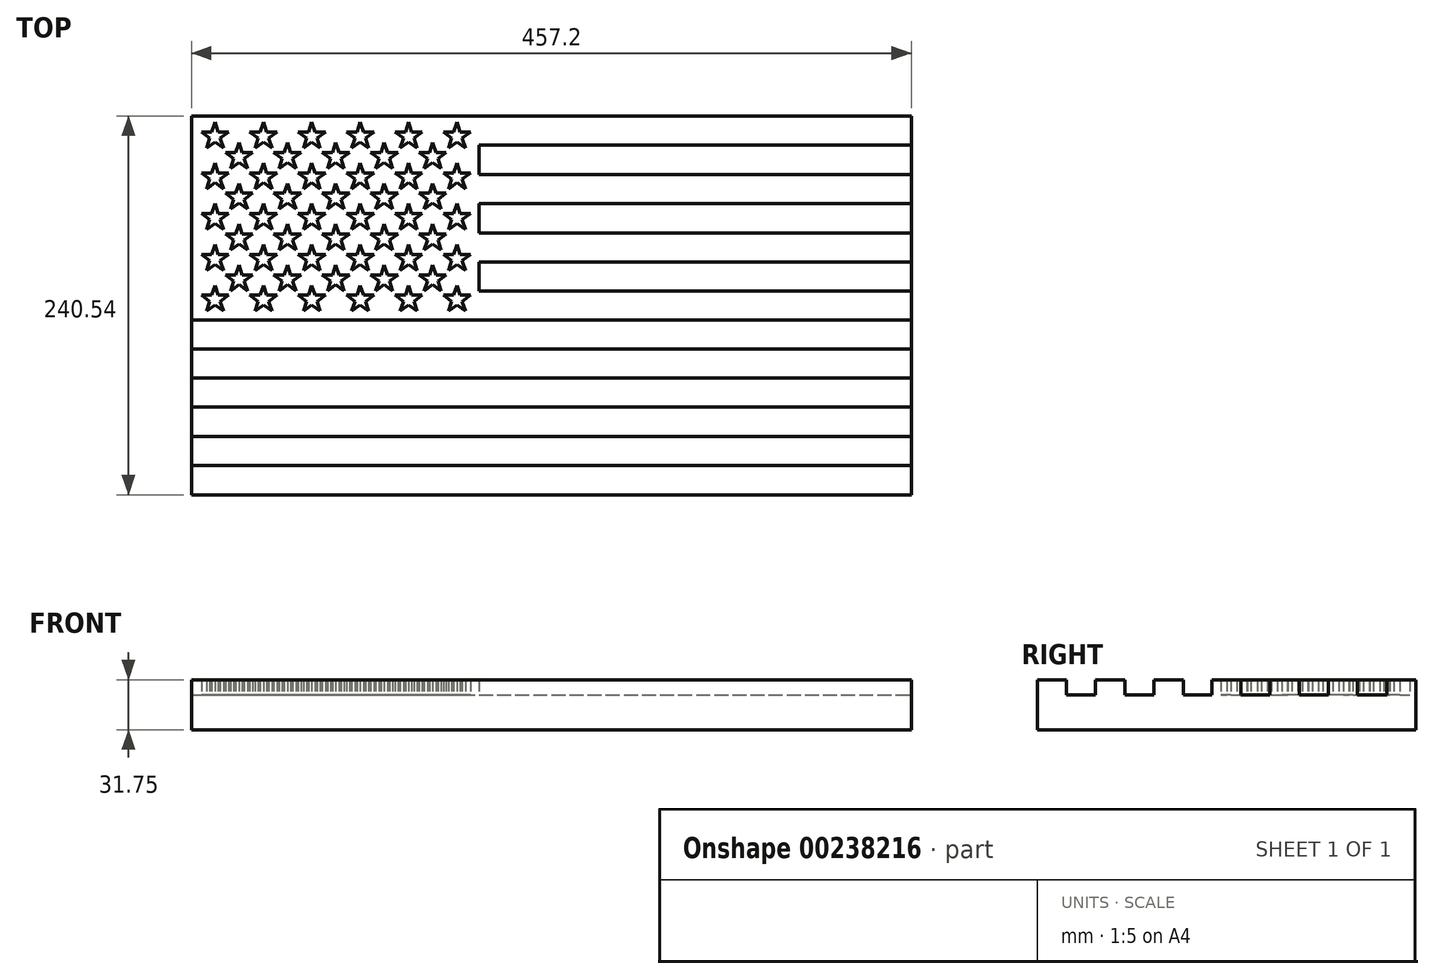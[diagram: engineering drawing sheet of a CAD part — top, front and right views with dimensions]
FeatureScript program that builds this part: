
annotation { "Feature Type Name" : "Feature", "Feature Type Description" : "" }
export const myFeature = defineFeature(function(context is Context, id is Id, definition is map)
    precondition{}
    {
        {
            var Q0;
            Q0=qCreatedBy(makeId("Top.planeOp"),FACE);
            var sketch = newSketch(context, id + "F0", { "sketchPlane" : qUnion([Q0])});
            skLineSegment(sketch, "E0.rect.bottom", {"start": v(228.6, 120.27) * mm, "end": v(-228.6, 120.27) * mm});
            skLineSegment(sketch, "E0.rect.top", {"start": v(228.6, -120.27) * mm, "end": v(-228.6, -120.27) * mm});
            skLineSegment(sketch, "E0.rect.left", {"start": v(228.6, 120.27) * mm, "end": v(228.6, -120.27) * mm});
            skLineSegment(sketch, "E0.rect.right", {"start": v(-228.6, 120.27) * mm, "end": v(-228.6, -120.27) * mm});
            skPoint(sketch, "E0.rect.middle", {"position": v(0, 0) * mm});
            skSolve(sketch);
        }
        {
            var Q0;
            Q0=qSketchRegion(id+"F0",true);
            extrude(context, id + "F1", {"entities" : qUnion([Q0]), "depth" : 22.22 * mm});
        }
        {
            var Q0;
            Q0=makeQuery(id+"F1.opExtrude","CAP_FACE",FACE,{"disambiguationData":[OSD([sQuery(id+"F0.wireOp",EDGE,"E0.rect.bottom"),sQuery(id+"F0.wireOp",EDGE,"E0.rect.top"),sQuery(id+"F0.wireOp",EDGE,"E0.rect.left"),sQuery(id+"F0.wireOp",EDGE,"E0.rect.right")])],"isStart":false});
            var sketch = newSketch(context, id + "F2", { "sketchPlane" : qUnion([Q0])});
            skLineSegment(sketch, "E1.bottom", {"start": v(-228.6, 120.27) * mm, "end": v(-45.97, 120.27) * mm});
            skLineSegment(sketch, "E1.top", {"start": v(-228.6, -9.25) * mm, "end": v(-45.97, -9.25) * mm});
            skLineSegment(sketch, "E1.left", {"start": v(-228.6, 120.27) * mm, "end": v(-228.6, -9.25) * mm});
            skLineSegment(sketch, "E1.right", {"start": v(-45.97, 120.27) * mm, "end": v(-45.97, -9.25) * mm});
            skLineSegment(sketch, "E2.bottom", {"start": v(-45.97, 120.27) * mm, "end": v(228.6, 120.27) * mm});
            skLineSegment(sketch, "E2.top", {"start": v(-45.97, 101.73) * mm, "end": v(228.6, 101.73) * mm});
            skLineSegment(sketch, "E2.left", {"start": v(-45.97, 120.27) * mm, "end": v(-45.97, 101.73) * mm});
            skLineSegment(sketch, "E2.right", {"start": v(228.6, 120.27) * mm, "end": v(228.6, 101.73) * mm});
            skLineSegment(sketch, "E3.MirrorCS", {"start": v(-45.97, 83.19) * mm, "end": v(228.6, 83.19) * mm});
            skLineSegment(sketch, "E4.MirrorCS", {"start": v(-45.97, 64.64) * mm, "end": v(228.6, 64.64) * mm});
            skLineSegment(sketch, "E5.MirrorCS", {"start": v(-45.97, 46.1) * mm, "end": v(228.6, 46.1) * mm});
            skLineSegment(sketch, "E6.MirrorCS", {"start": v(-45.97, 27.56) * mm, "end": v(228.6, 27.56) * mm});
            skLineSegment(sketch, "E7.MirrorCS", {"start": v(-45.97, 9.02) * mm, "end": v(228.6, 9.02) * mm});
            skLineSegment(sketch, "E8", {"start": v(-45.97, -9.25) * mm, "end": v(228.6, -9.25) * mm});
            skLineSegment(sketch, "E9.bottom", {"start": v(-228.6, -120.27) * mm, "end": v(228.6, -120.27) * mm});
            skLineSegment(sketch, "E9.top", {"start": v(-228.6, -101.73) * mm, "end": v(228.6, -101.73) * mm});
            skLineSegment(sketch, "E9.left", {"start": v(-228.6, -120.27) * mm, "end": v(-228.6, -101.73) * mm});
            skLineSegment(sketch, "E9.right", {"start": v(228.6, -120.27) * mm, "end": v(228.6, -101.73) * mm});
            skLineSegment(sketch, "E10.MirrorCS", {"start": v(-228.6, -83.19) * mm, "end": v(228.6, -83.19) * mm});
            skLineSegment(sketch, "E11.MirrorCS", {"start": v(-228.6, -64.64) * mm, "end": v(228.6, -64.64) * mm});
            skLineSegment(sketch, "E12.MirrorCS", {"start": v(-228.6, -46.1) * mm, "end": v(228.6, -46.1) * mm});
            skLineSegment(sketch, "E13.MirrorCS", {"start": v(-228.6, -27.56) * mm, "end": v(228.6, -27.56) * mm});
            skLineSegment(sketch, "E14.bottom", {"start": v(-228.6, 120.27) * mm, "end": v(-213.61, 120.27) * mm});
            skLineSegment(sketch, "E14.left", {"start": v(-228.6, 120.27) * mm, "end": v(-228.6, 107.31) * mm});
            skLineSegment(sketch, "E15.trimOffspring", {"start": v(-210.03, 108.18) * mm, "end": v(-210.03, 108.18) * mm});
            skLineSegment(sketch, "E16", {"start": v(-222.27, 110.13) * mm, "end": v(-215.66, 110.13) * mm});
            skLineSegment(sketch, "E17", {"start": v(-204.95, 110.13) * mm, "end": v(-210.3, 106.24) * mm});
            skLineSegment(sketch, "E18", {"start": v(-218.97, 99.95) * mm, "end": v(-216.92, 106.24) * mm});
            skLineSegment(sketch, "E19", {"start": v(-213.61, 116.42) * mm, "end": v(-211.57, 110.13) * mm});
            skLineSegment(sketch, "E20", {"start": v(-208.26, 99.95) * mm, "end": v(-213.61, 103.84) * mm});
            skLineSegment(sketch, "E21.trimOffspring", {"start": v(-210.3, 106.24) * mm, "end": v(-208.26, 99.95) * mm});
            skLineSegment(sketch, "E22.trimOffspring", {"start": v(-211.57, 110.13) * mm, "end": v(-204.95, 110.13) * mm});
            skLineSegment(sketch, "E23.trimOffspring", {"start": v(-215.66, 110.13) * mm, "end": v(-213.61, 116.42) * mm});
            skLineSegment(sketch, "E24.trimOffspring", {"start": v(-216.92, 106.24) * mm, "end": v(-222.27, 110.13) * mm});
            skLineSegment(sketch, "E25.trimOffspring", {"start": v(-213.61, 103.84) * mm, "end": v(-218.97, 99.95) * mm});
            skLineSegment(sketch, "E26.0.1.0", {"start": v(-218.97, 74.04) * mm, "end": v(-216.92, 80.33) * mm});
            skLineSegment(sketch, "E26.0.1.1", {"start": v(-210.3, 80.33) * mm, "end": v(-208.26, 74.04) * mm});
            skLineSegment(sketch, "E26.0.1.2", {"start": v(-211.57, 84.22) * mm, "end": v(-204.95, 84.22) * mm});
            skLineSegment(sketch, "E26.0.1.3", {"start": v(-216.92, 80.33) * mm, "end": v(-222.27, 84.22) * mm});
            skLineSegment(sketch, "E26.0.1.4", {"start": v(-213.61, 77.93) * mm, "end": v(-218.97, 74.04) * mm});
            skLineSegment(sketch, "E26.0.1.5", {"start": v(-213.61, 90.51) * mm, "end": v(-211.57, 84.22) * mm});
            skLineSegment(sketch, "E26.0.1.6", {"start": v(-215.66, 84.22) * mm, "end": v(-213.61, 90.51) * mm});
            skLineSegment(sketch, "E26.0.1.7", {"start": v(-222.27, 84.22) * mm, "end": v(-215.66, 84.22) * mm});
            skLineSegment(sketch, "E26.0.1.8", {"start": v(-208.26, 74.04) * mm, "end": v(-213.61, 77.93) * mm});
            skLineSegment(sketch, "E26.0.1.9", {"start": v(-204.95, 84.22) * mm, "end": v(-210.3, 80.33) * mm});
            skLineSegment(sketch, "E26.0.2.0", {"start": v(-218.97, 48.13) * mm, "end": v(-216.92, 54.42) * mm});
            skLineSegment(sketch, "E26.0.2.1", {"start": v(-210.3, 54.42) * mm, "end": v(-208.26, 48.13) * mm});
            skLineSegment(sketch, "E26.0.2.2", {"start": v(-211.57, 58.31) * mm, "end": v(-204.95, 58.31) * mm});
            skLineSegment(sketch, "E26.0.2.3", {"start": v(-216.92, 54.42) * mm, "end": v(-222.27, 58.31) * mm});
            skLineSegment(sketch, "E26.0.2.4", {"start": v(-213.61, 52.02) * mm, "end": v(-218.97, 48.13) * mm});
            skLineSegment(sketch, "E26.0.2.5", {"start": v(-213.61, 64.6) * mm, "end": v(-211.57, 58.31) * mm});
            skLineSegment(sketch, "E26.0.2.6", {"start": v(-215.66, 58.31) * mm, "end": v(-213.61, 64.6) * mm});
            skLineSegment(sketch, "E26.0.2.7", {"start": v(-222.27, 58.31) * mm, "end": v(-215.66, 58.31) * mm});
            skLineSegment(sketch, "E26.0.2.8", {"start": v(-208.26, 48.13) * mm, "end": v(-213.61, 52.02) * mm});
            skLineSegment(sketch, "E26.0.2.9", {"start": v(-204.95, 58.31) * mm, "end": v(-210.3, 54.42) * mm});
            skLineSegment(sketch, "E26.0.3.0", {"start": v(-218.97, 22.23) * mm, "end": v(-216.92, 28.52) * mm});
            skLineSegment(sketch, "E26.0.3.1", {"start": v(-210.3, 28.52) * mm, "end": v(-208.26, 22.23) * mm});
            skLineSegment(sketch, "E26.0.3.2", {"start": v(-211.57, 32.4) * mm, "end": v(-204.95, 32.4) * mm});
            skLineSegment(sketch, "E26.0.3.3", {"start": v(-216.92, 28.52) * mm, "end": v(-222.27, 32.4) * mm});
            skLineSegment(sketch, "E26.0.3.4", {"start": v(-213.61, 26.11) * mm, "end": v(-218.97, 22.23) * mm});
            skLineSegment(sketch, "E26.0.3.5", {"start": v(-213.61, 38.7) * mm, "end": v(-211.57, 32.4) * mm});
            skLineSegment(sketch, "E26.0.3.6", {"start": v(-215.66, 32.4) * mm, "end": v(-213.61, 38.7) * mm});
            skLineSegment(sketch, "E26.0.3.7", {"start": v(-222.27, 32.4) * mm, "end": v(-215.66, 32.4) * mm});
            skLineSegment(sketch, "E26.0.3.8", {"start": v(-208.26, 22.23) * mm, "end": v(-213.61, 26.11) * mm});
            skLineSegment(sketch, "E26.0.3.9", {"start": v(-204.95, 32.4) * mm, "end": v(-210.3, 28.52) * mm});
            skLineSegment(sketch, "E26.0.4.0", {"start": v(-218.97, -3.68) * mm, "end": v(-216.92, 2.6) * mm});
            skLineSegment(sketch, "E26.0.4.1", {"start": v(-210.3, 2.6) * mm, "end": v(-208.26, -3.68) * mm});
            skLineSegment(sketch, "E26.0.4.2", {"start": v(-211.57, 6.5) * mm, "end": v(-204.95, 6.5) * mm});
            skLineSegment(sketch, "E26.0.4.3", {"start": v(-216.92, 2.6) * mm, "end": v(-222.27, 6.5) * mm});
            skLineSegment(sketch, "E26.0.4.4", {"start": v(-213.61, 0.2) * mm, "end": v(-218.97, -3.68) * mm});
            skLineSegment(sketch, "E26.0.4.5", {"start": v(-213.61, 12.79) * mm, "end": v(-211.57, 6.5) * mm});
            skLineSegment(sketch, "E26.0.4.6", {"start": v(-215.66, 6.5) * mm, "end": v(-213.61, 12.79) * mm});
            skLineSegment(sketch, "E26.0.4.7", {"start": v(-222.27, 6.5) * mm, "end": v(-215.66, 6.5) * mm});
            skLineSegment(sketch, "E26.0.4.8", {"start": v(-208.26, -3.68) * mm, "end": v(-213.61, 0.2) * mm});
            skLineSegment(sketch, "E26.0.4.9", {"start": v(-204.95, 6.5) * mm, "end": v(-210.3, 2.6) * mm});
            skLineSegment(sketch, "E26.1.0.0", {"start": v(-188.23, 99.95) * mm, "end": v(-186.19, 106.24) * mm});
            skLineSegment(sketch, "E26.1.0.1", {"start": v(-179.57, 106.24) * mm, "end": v(-177.53, 99.95) * mm});
            skLineSegment(sketch, "E26.1.0.2", {"start": v(-180.84, 110.13) * mm, "end": v(-174.22, 110.13) * mm});
            skLineSegment(sketch, "E26.1.0.3", {"start": v(-186.19, 106.24) * mm, "end": v(-191.54, 110.13) * mm});
            skLineSegment(sketch, "E26.1.0.4", {"start": v(-182.88, 103.84) * mm, "end": v(-188.23, 99.95) * mm});
            skLineSegment(sketch, "E26.1.0.5", {"start": v(-182.88, 116.42) * mm, "end": v(-180.84, 110.13) * mm});
            skLineSegment(sketch, "E26.1.0.6", {"start": v(-184.92, 110.13) * mm, "end": v(-182.88, 116.42) * mm});
            skLineSegment(sketch, "E26.1.0.7", {"start": v(-191.54, 110.13) * mm, "end": v(-184.92, 110.13) * mm});
            skLineSegment(sketch, "E26.1.0.8", {"start": v(-177.53, 99.95) * mm, "end": v(-182.88, 103.84) * mm});
            skLineSegment(sketch, "E26.1.0.9", {"start": v(-174.22, 110.13) * mm, "end": v(-179.57, 106.24) * mm});
            skLineSegment(sketch, "E26.1.1.0", {"start": v(-188.23, 74.04) * mm, "end": v(-186.19, 80.33) * mm});
            skLineSegment(sketch, "E26.1.1.1", {"start": v(-179.57, 80.33) * mm, "end": v(-177.53, 74.04) * mm});
            skLineSegment(sketch, "E26.1.1.2", {"start": v(-180.84, 84.22) * mm, "end": v(-174.22, 84.22) * mm});
            skLineSegment(sketch, "E26.1.1.3", {"start": v(-186.19, 80.33) * mm, "end": v(-191.54, 84.22) * mm});
            skLineSegment(sketch, "E26.1.1.4", {"start": v(-182.88, 77.93) * mm, "end": v(-188.23, 74.04) * mm});
            skLineSegment(sketch, "E26.1.1.5", {"start": v(-182.88, 90.51) * mm, "end": v(-180.84, 84.22) * mm});
            skLineSegment(sketch, "E26.1.1.6", {"start": v(-184.92, 84.22) * mm, "end": v(-182.88, 90.51) * mm});
            skLineSegment(sketch, "E26.1.1.7", {"start": v(-191.54, 84.22) * mm, "end": v(-184.92, 84.22) * mm});
            skLineSegment(sketch, "E26.1.1.8", {"start": v(-177.53, 74.04) * mm, "end": v(-182.88, 77.93) * mm});
            skLineSegment(sketch, "E26.1.1.9", {"start": v(-174.22, 84.22) * mm, "end": v(-179.57, 80.33) * mm});
            skLineSegment(sketch, "E26.1.2.0", {"start": v(-188.23, 48.13) * mm, "end": v(-186.19, 54.42) * mm});
            skLineSegment(sketch, "E26.1.2.1", {"start": v(-179.57, 54.42) * mm, "end": v(-177.53, 48.13) * mm});
            skLineSegment(sketch, "E26.1.2.2", {"start": v(-180.84, 58.31) * mm, "end": v(-174.22, 58.31) * mm});
            skLineSegment(sketch, "E26.1.2.3", {"start": v(-186.19, 54.42) * mm, "end": v(-191.54, 58.31) * mm});
            skLineSegment(sketch, "E26.1.2.4", {"start": v(-182.88, 52.02) * mm, "end": v(-188.23, 48.13) * mm});
            skLineSegment(sketch, "E26.1.2.5", {"start": v(-182.88, 64.6) * mm, "end": v(-180.84, 58.31) * mm});
            skLineSegment(sketch, "E26.1.2.6", {"start": v(-184.92, 58.31) * mm, "end": v(-182.88, 64.6) * mm});
            skLineSegment(sketch, "E26.1.2.7", {"start": v(-191.54, 58.31) * mm, "end": v(-184.92, 58.31) * mm});
            skLineSegment(sketch, "E26.1.2.8", {"start": v(-177.53, 48.13) * mm, "end": v(-182.88, 52.02) * mm});
            skLineSegment(sketch, "E26.1.2.9", {"start": v(-174.22, 58.31) * mm, "end": v(-179.57, 54.42) * mm});
            skLineSegment(sketch, "E26.1.3.0", {"start": v(-188.23, 22.23) * mm, "end": v(-186.19, 28.52) * mm});
            skLineSegment(sketch, "E26.1.3.1", {"start": v(-179.57, 28.52) * mm, "end": v(-177.53, 22.23) * mm});
            skLineSegment(sketch, "E26.1.3.2", {"start": v(-180.84, 32.4) * mm, "end": v(-174.22, 32.4) * mm});
            skLineSegment(sketch, "E26.1.3.3", {"start": v(-186.19, 28.52) * mm, "end": v(-191.54, 32.4) * mm});
            skLineSegment(sketch, "E26.1.3.4", {"start": v(-182.88, 26.11) * mm, "end": v(-188.23, 22.23) * mm});
            skLineSegment(sketch, "E26.1.3.5", {"start": v(-182.88, 38.7) * mm, "end": v(-180.84, 32.4) * mm});
            skLineSegment(sketch, "E26.1.3.6", {"start": v(-184.92, 32.4) * mm, "end": v(-182.88, 38.7) * mm});
            skLineSegment(sketch, "E26.1.3.7", {"start": v(-191.54, 32.4) * mm, "end": v(-184.92, 32.4) * mm});
            skLineSegment(sketch, "E26.1.3.8", {"start": v(-177.53, 22.23) * mm, "end": v(-182.88, 26.11) * mm});
            skLineSegment(sketch, "E26.1.3.9", {"start": v(-174.22, 32.4) * mm, "end": v(-179.57, 28.52) * mm});
            skLineSegment(sketch, "E26.1.4.0", {"start": v(-188.23, -3.68) * mm, "end": v(-186.19, 2.6) * mm});
            skLineSegment(sketch, "E26.1.4.1", {"start": v(-179.57, 2.6) * mm, "end": v(-177.53, -3.68) * mm});
            skLineSegment(sketch, "E26.1.4.2", {"start": v(-180.84, 6.5) * mm, "end": v(-174.22, 6.5) * mm});
            skLineSegment(sketch, "E26.1.4.3", {"start": v(-186.19, 2.6) * mm, "end": v(-191.54, 6.5) * mm});
            skLineSegment(sketch, "E26.1.4.4", {"start": v(-182.88, 0.2) * mm, "end": v(-188.23, -3.68) * mm});
            skLineSegment(sketch, "E26.1.4.5", {"start": v(-182.88, 12.79) * mm, "end": v(-180.84, 6.5) * mm});
            skLineSegment(sketch, "E26.1.4.6", {"start": v(-184.92, 6.5) * mm, "end": v(-182.88, 12.79) * mm});
            skLineSegment(sketch, "E26.1.4.7", {"start": v(-191.54, 6.5) * mm, "end": v(-184.92, 6.5) * mm});
            skLineSegment(sketch, "E26.1.4.8", {"start": v(-177.53, -3.68) * mm, "end": v(-182.88, 0.2) * mm});
            skLineSegment(sketch, "E26.1.4.9", {"start": v(-174.22, 6.5) * mm, "end": v(-179.57, 2.6) * mm});
            skLineSegment(sketch, "E26.2.0.0", {"start": v(-157.5, 99.95) * mm, "end": v(-155.45, 106.24) * mm});
            skLineSegment(sketch, "E26.2.0.1", {"start": v(-148.84, 106.24) * mm, "end": v(-146.8, 99.95) * mm});
            skLineSegment(sketch, "E26.2.0.2", {"start": v(-150.1, 110.13) * mm, "end": v(-143.49, 110.13) * mm});
            skLineSegment(sketch, "E26.2.0.3", {"start": v(-155.45, 106.24) * mm, "end": v(-160.8, 110.13) * mm});
            skLineSegment(sketch, "E26.2.0.4", {"start": v(-152.15, 103.84) * mm, "end": v(-157.5, 99.95) * mm});
            skLineSegment(sketch, "E26.2.0.5", {"start": v(-152.15, 116.42) * mm, "end": v(-150.1, 110.13) * mm});
            skLineSegment(sketch, "E26.2.0.6", {"start": v(-154.2, 110.13) * mm, "end": v(-152.15, 116.42) * mm});
            skLineSegment(sketch, "E26.2.0.7", {"start": v(-160.8, 110.13) * mm, "end": v(-154.2, 110.13) * mm});
            skLineSegment(sketch, "E26.2.0.8", {"start": v(-146.8, 99.95) * mm, "end": v(-152.15, 103.84) * mm});
            skLineSegment(sketch, "E26.2.0.9", {"start": v(-143.49, 110.13) * mm, "end": v(-148.84, 106.24) * mm});
            skLineSegment(sketch, "E26.2.1.0", {"start": v(-157.5, 74.04) * mm, "end": v(-155.45, 80.33) * mm});
            skLineSegment(sketch, "E26.2.1.1", {"start": v(-148.84, 80.33) * mm, "end": v(-146.8, 74.04) * mm});
            skLineSegment(sketch, "E26.2.1.2", {"start": v(-150.1, 84.22) * mm, "end": v(-143.49, 84.22) * mm});
            skLineSegment(sketch, "E26.2.1.3", {"start": v(-155.45, 80.33) * mm, "end": v(-160.8, 84.22) * mm});
            skLineSegment(sketch, "E26.2.1.4", {"start": v(-152.15, 77.93) * mm, "end": v(-157.5, 74.04) * mm});
            skLineSegment(sketch, "E26.2.1.5", {"start": v(-152.15, 90.51) * mm, "end": v(-150.1, 84.22) * mm});
            skLineSegment(sketch, "E26.2.1.6", {"start": v(-154.2, 84.22) * mm, "end": v(-152.15, 90.51) * mm});
            skLineSegment(sketch, "E26.2.1.7", {"start": v(-160.8, 84.22) * mm, "end": v(-154.2, 84.22) * mm});
            skLineSegment(sketch, "E26.2.1.8", {"start": v(-146.8, 74.04) * mm, "end": v(-152.15, 77.93) * mm});
            skLineSegment(sketch, "E26.2.1.9", {"start": v(-143.49, 84.22) * mm, "end": v(-148.84, 80.33) * mm});
            skLineSegment(sketch, "E26.2.2.0", {"start": v(-157.5, 48.13) * mm, "end": v(-155.45, 54.42) * mm});
            skLineSegment(sketch, "E26.2.2.1", {"start": v(-148.84, 54.42) * mm, "end": v(-146.8, 48.13) * mm});
            skLineSegment(sketch, "E26.2.2.2", {"start": v(-150.1, 58.31) * mm, "end": v(-143.49, 58.31) * mm});
            skLineSegment(sketch, "E26.2.2.3", {"start": v(-155.45, 54.42) * mm, "end": v(-160.8, 58.31) * mm});
            skLineSegment(sketch, "E26.2.2.4", {"start": v(-152.15, 52.02) * mm, "end": v(-157.5, 48.13) * mm});
            skLineSegment(sketch, "E26.2.2.5", {"start": v(-152.15, 64.6) * mm, "end": v(-150.1, 58.31) * mm});
            skLineSegment(sketch, "E26.2.2.6", {"start": v(-154.2, 58.31) * mm, "end": v(-152.15, 64.6) * mm});
            skLineSegment(sketch, "E26.2.2.7", {"start": v(-160.8, 58.31) * mm, "end": v(-154.2, 58.31) * mm});
            skLineSegment(sketch, "E26.2.2.8", {"start": v(-146.8, 48.13) * mm, "end": v(-152.15, 52.02) * mm});
            skLineSegment(sketch, "E26.2.2.9", {"start": v(-143.49, 58.31) * mm, "end": v(-148.84, 54.42) * mm});
            skLineSegment(sketch, "E26.2.3.0", {"start": v(-157.5, 22.23) * mm, "end": v(-155.45, 28.52) * mm});
            skLineSegment(sketch, "E26.2.3.1", {"start": v(-148.84, 28.52) * mm, "end": v(-146.8, 22.23) * mm});
            skLineSegment(sketch, "E26.2.3.2", {"start": v(-150.1, 32.4) * mm, "end": v(-143.49, 32.4) * mm});
            skLineSegment(sketch, "E26.2.3.3", {"start": v(-155.45, 28.52) * mm, "end": v(-160.8, 32.4) * mm});
            skLineSegment(sketch, "E26.2.3.4", {"start": v(-152.15, 26.11) * mm, "end": v(-157.5, 22.23) * mm});
            skLineSegment(sketch, "E26.2.3.5", {"start": v(-152.15, 38.7) * mm, "end": v(-150.1, 32.4) * mm});
            skLineSegment(sketch, "E26.2.3.6", {"start": v(-154.2, 32.4) * mm, "end": v(-152.15, 38.7) * mm});
            skLineSegment(sketch, "E26.2.3.7", {"start": v(-160.8, 32.4) * mm, "end": v(-154.2, 32.4) * mm});
            skLineSegment(sketch, "E26.2.3.8", {"start": v(-146.8, 22.23) * mm, "end": v(-152.15, 26.11) * mm});
            skLineSegment(sketch, "E26.2.3.9", {"start": v(-143.49, 32.4) * mm, "end": v(-148.84, 28.52) * mm});
            skLineSegment(sketch, "E26.2.4.0", {"start": v(-157.5, -3.68) * mm, "end": v(-155.45, 2.6) * mm});
            skLineSegment(sketch, "E26.2.4.1", {"start": v(-148.84, 2.6) * mm, "end": v(-146.8, -3.68) * mm});
            skLineSegment(sketch, "E26.2.4.2", {"start": v(-150.1, 6.5) * mm, "end": v(-143.49, 6.5) * mm});
            skLineSegment(sketch, "E26.2.4.3", {"start": v(-155.45, 2.6) * mm, "end": v(-160.8, 6.5) * mm});
            skLineSegment(sketch, "E26.2.4.4", {"start": v(-152.15, 0.2) * mm, "end": v(-157.5, -3.68) * mm});
            skLineSegment(sketch, "E26.2.4.5", {"start": v(-152.15, 12.79) * mm, "end": v(-150.1, 6.5) * mm});
            skLineSegment(sketch, "E26.2.4.6", {"start": v(-154.2, 6.5) * mm, "end": v(-152.15, 12.79) * mm});
            skLineSegment(sketch, "E26.2.4.7", {"start": v(-160.8, 6.5) * mm, "end": v(-154.2, 6.5) * mm});
            skLineSegment(sketch, "E26.2.4.8", {"start": v(-146.8, -3.68) * mm, "end": v(-152.15, 0.2) * mm});
            skLineSegment(sketch, "E26.2.4.9", {"start": v(-143.49, 6.5) * mm, "end": v(-148.84, 2.6) * mm});
            skLineSegment(sketch, "E26.3.0.0", {"start": v(-126.76, 99.95) * mm, "end": v(-124.72, 106.24) * mm});
            skLineSegment(sketch, "E26.3.0.1", {"start": v(-118.1, 106.24) * mm, "end": v(-116.06, 99.95) * mm});
            skLineSegment(sketch, "E26.3.0.2", {"start": v(-119.37, 110.13) * mm, "end": v(-112.75, 110.13) * mm});
            skLineSegment(sketch, "E26.3.0.3", {"start": v(-124.72, 106.24) * mm, "end": v(-130.07, 110.13) * mm});
            skLineSegment(sketch, "E26.3.0.4", {"start": v(-121.41, 103.84) * mm, "end": v(-126.76, 99.95) * mm});
            skLineSegment(sketch, "E26.3.0.5", {"start": v(-121.41, 116.42) * mm, "end": v(-119.37, 110.13) * mm});
            skLineSegment(sketch, "E26.3.0.6", {"start": v(-123.46, 110.13) * mm, "end": v(-121.41, 116.42) * mm});
            skLineSegment(sketch, "E26.3.0.7", {"start": v(-130.07, 110.13) * mm, "end": v(-123.46, 110.13) * mm});
            skLineSegment(sketch, "E26.3.0.8", {"start": v(-116.06, 99.95) * mm, "end": v(-121.41, 103.84) * mm});
            skLineSegment(sketch, "E26.3.0.9", {"start": v(-112.75, 110.13) * mm, "end": v(-118.1, 106.24) * mm});
            skLineSegment(sketch, "E26.3.1.0", {"start": v(-126.76, 74.04) * mm, "end": v(-124.72, 80.33) * mm});
            skLineSegment(sketch, "E26.3.1.1", {"start": v(-118.1, 80.33) * mm, "end": v(-116.06, 74.04) * mm});
            skLineSegment(sketch, "E26.3.1.2", {"start": v(-119.37, 84.22) * mm, "end": v(-112.75, 84.22) * mm});
            skLineSegment(sketch, "E26.3.1.3", {"start": v(-124.72, 80.33) * mm, "end": v(-130.07, 84.22) * mm});
            skLineSegment(sketch, "E26.3.1.4", {"start": v(-121.41, 77.93) * mm, "end": v(-126.76, 74.04) * mm});
            skLineSegment(sketch, "E26.3.1.5", {"start": v(-121.41, 90.51) * mm, "end": v(-119.37, 84.22) * mm});
            skLineSegment(sketch, "E26.3.1.6", {"start": v(-123.46, 84.22) * mm, "end": v(-121.41, 90.51) * mm});
            skLineSegment(sketch, "E26.3.1.7", {"start": v(-130.07, 84.22) * mm, "end": v(-123.46, 84.22) * mm});
            skLineSegment(sketch, "E26.3.1.8", {"start": v(-116.06, 74.04) * mm, "end": v(-121.41, 77.93) * mm});
            skLineSegment(sketch, "E26.3.1.9", {"start": v(-112.75, 84.22) * mm, "end": v(-118.1, 80.33) * mm});
            skLineSegment(sketch, "E26.3.2.0", {"start": v(-126.76, 48.13) * mm, "end": v(-124.72, 54.42) * mm});
            skLineSegment(sketch, "E26.3.2.1", {"start": v(-118.1, 54.42) * mm, "end": v(-116.06, 48.13) * mm});
            skLineSegment(sketch, "E26.3.2.2", {"start": v(-119.37, 58.31) * mm, "end": v(-112.75, 58.31) * mm});
            skLineSegment(sketch, "E26.3.2.3", {"start": v(-124.72, 54.42) * mm, "end": v(-130.07, 58.31) * mm});
            skLineSegment(sketch, "E26.3.2.4", {"start": v(-121.41, 52.02) * mm, "end": v(-126.76, 48.13) * mm});
            skLineSegment(sketch, "E26.3.2.5", {"start": v(-121.41, 64.6) * mm, "end": v(-119.37, 58.31) * mm});
            skLineSegment(sketch, "E26.3.2.6", {"start": v(-123.46, 58.31) * mm, "end": v(-121.41, 64.6) * mm});
            skLineSegment(sketch, "E26.3.2.7", {"start": v(-130.07, 58.31) * mm, "end": v(-123.46, 58.31) * mm});
            skLineSegment(sketch, "E26.3.2.8", {"start": v(-116.06, 48.13) * mm, "end": v(-121.41, 52.02) * mm});
            skLineSegment(sketch, "E26.3.2.9", {"start": v(-112.75, 58.31) * mm, "end": v(-118.1, 54.42) * mm});
            skLineSegment(sketch, "E26.3.3.0", {"start": v(-126.76, 22.23) * mm, "end": v(-124.72, 28.52) * mm});
            skLineSegment(sketch, "E26.3.3.1", {"start": v(-118.1, 28.52) * mm, "end": v(-116.06, 22.23) * mm});
            skLineSegment(sketch, "E26.3.3.2", {"start": v(-119.37, 32.4) * mm, "end": v(-112.75, 32.4) * mm});
            skLineSegment(sketch, "E26.3.3.3", {"start": v(-124.72, 28.52) * mm, "end": v(-130.07, 32.4) * mm});
            skLineSegment(sketch, "E26.3.3.4", {"start": v(-121.41, 26.11) * mm, "end": v(-126.76, 22.23) * mm});
            skLineSegment(sketch, "E26.3.3.5", {"start": v(-121.41, 38.7) * mm, "end": v(-119.37, 32.4) * mm});
            skLineSegment(sketch, "E26.3.3.6", {"start": v(-123.46, 32.4) * mm, "end": v(-121.41, 38.7) * mm});
            skLineSegment(sketch, "E26.3.3.7", {"start": v(-130.07, 32.4) * mm, "end": v(-123.46, 32.4) * mm});
            skLineSegment(sketch, "E26.3.3.8", {"start": v(-116.06, 22.23) * mm, "end": v(-121.41, 26.11) * mm});
            skLineSegment(sketch, "E26.3.3.9", {"start": v(-112.75, 32.4) * mm, "end": v(-118.1, 28.52) * mm});
            skLineSegment(sketch, "E26.3.4.0", {"start": v(-126.76, -3.68) * mm, "end": v(-124.72, 2.6) * mm});
            skLineSegment(sketch, "E26.3.4.1", {"start": v(-118.1, 2.6) * mm, "end": v(-116.06, -3.68) * mm});
            skLineSegment(sketch, "E26.3.4.2", {"start": v(-119.37, 6.5) * mm, "end": v(-112.75, 6.5) * mm});
            skLineSegment(sketch, "E26.3.4.3", {"start": v(-124.72, 2.6) * mm, "end": v(-130.07, 6.5) * mm});
            skLineSegment(sketch, "E26.3.4.4", {"start": v(-121.41, 0.2) * mm, "end": v(-126.76, -3.68) * mm});
            skLineSegment(sketch, "E26.3.4.5", {"start": v(-121.41, 12.79) * mm, "end": v(-119.37, 6.5) * mm});
            skLineSegment(sketch, "E26.3.4.6", {"start": v(-123.46, 6.5) * mm, "end": v(-121.41, 12.79) * mm});
            skLineSegment(sketch, "E26.3.4.7", {"start": v(-130.07, 6.5) * mm, "end": v(-123.46, 6.5) * mm});
            skLineSegment(sketch, "E26.3.4.8", {"start": v(-116.06, -3.68) * mm, "end": v(-121.41, 0.2) * mm});
            skLineSegment(sketch, "E26.3.4.9", {"start": v(-112.75, 6.5) * mm, "end": v(-118.1, 2.6) * mm});
            skLineSegment(sketch, "E26.4.0.0", {"start": v(-96.03, 99.95) * mm, "end": v(-93.99, 106.24) * mm});
            skLineSegment(sketch, "E26.4.0.1", {"start": v(-87.37, 106.24) * mm, "end": v(-85.33, 99.95) * mm});
            skLineSegment(sketch, "E26.4.0.2", {"start": v(-88.63, 110.13) * mm, "end": v(-82.02, 110.13) * mm});
            skLineSegment(sketch, "E26.4.0.3", {"start": v(-93.99, 106.24) * mm, "end": v(-99.34, 110.13) * mm});
            skLineSegment(sketch, "E26.4.0.4", {"start": v(-90.68, 103.84) * mm, "end": v(-96.03, 99.95) * mm});
            skLineSegment(sketch, "E26.4.0.5", {"start": v(-90.68, 116.42) * mm, "end": v(-88.63, 110.13) * mm});
            skLineSegment(sketch, "E26.4.0.6", {"start": v(-92.72, 110.13) * mm, "end": v(-90.68, 116.42) * mm});
            skLineSegment(sketch, "E26.4.0.7", {"start": v(-99.34, 110.13) * mm, "end": v(-92.72, 110.13) * mm});
            skLineSegment(sketch, "E26.4.0.8", {"start": v(-85.33, 99.95) * mm, "end": v(-90.68, 103.84) * mm});
            skLineSegment(sketch, "E26.4.0.9", {"start": v(-82.02, 110.13) * mm, "end": v(-87.37, 106.24) * mm});
            skLineSegment(sketch, "E26.4.1.0", {"start": v(-96.03, 74.04) * mm, "end": v(-93.99, 80.33) * mm});
            skLineSegment(sketch, "E26.4.1.1", {"start": v(-87.37, 80.33) * mm, "end": v(-85.33, 74.04) * mm});
            skLineSegment(sketch, "E26.4.1.2", {"start": v(-88.63, 84.22) * mm, "end": v(-82.02, 84.22) * mm});
            skLineSegment(sketch, "E26.4.1.3", {"start": v(-93.99, 80.33) * mm, "end": v(-99.34, 84.22) * mm});
            skLineSegment(sketch, "E26.4.1.4", {"start": v(-90.68, 77.93) * mm, "end": v(-96.03, 74.04) * mm});
            skLineSegment(sketch, "E26.4.1.5", {"start": v(-90.68, 90.51) * mm, "end": v(-88.63, 84.22) * mm});
            skLineSegment(sketch, "E26.4.1.6", {"start": v(-92.72, 84.22) * mm, "end": v(-90.68, 90.51) * mm});
            skLineSegment(sketch, "E26.4.1.7", {"start": v(-99.34, 84.22) * mm, "end": v(-92.72, 84.22) * mm});
            skLineSegment(sketch, "E26.4.1.8", {"start": v(-85.33, 74.04) * mm, "end": v(-90.68, 77.93) * mm});
            skLineSegment(sketch, "E26.4.1.9", {"start": v(-82.02, 84.22) * mm, "end": v(-87.37, 80.33) * mm});
            skLineSegment(sketch, "E26.4.2.0", {"start": v(-96.03, 48.13) * mm, "end": v(-93.99, 54.42) * mm});
            skLineSegment(sketch, "E26.4.2.1", {"start": v(-87.37, 54.42) * mm, "end": v(-85.33, 48.13) * mm});
            skLineSegment(sketch, "E26.4.2.2", {"start": v(-88.63, 58.31) * mm, "end": v(-82.02, 58.31) * mm});
            skLineSegment(sketch, "E26.4.2.3", {"start": v(-93.99, 54.42) * mm, "end": v(-99.34, 58.31) * mm});
            skLineSegment(sketch, "E26.4.2.4", {"start": v(-90.68, 52.02) * mm, "end": v(-96.03, 48.13) * mm});
            skLineSegment(sketch, "E26.4.2.5", {"start": v(-90.68, 64.6) * mm, "end": v(-88.63, 58.31) * mm});
            skLineSegment(sketch, "E26.4.2.6", {"start": v(-92.72, 58.31) * mm, "end": v(-90.68, 64.6) * mm});
            skLineSegment(sketch, "E26.4.2.7", {"start": v(-99.34, 58.31) * mm, "end": v(-92.72, 58.31) * mm});
            skLineSegment(sketch, "E26.4.2.8", {"start": v(-85.33, 48.13) * mm, "end": v(-90.68, 52.02) * mm});
            skLineSegment(sketch, "E26.4.2.9", {"start": v(-82.02, 58.31) * mm, "end": v(-87.37, 54.42) * mm});
            skLineSegment(sketch, "E26.4.3.0", {"start": v(-96.03, 22.23) * mm, "end": v(-93.99, 28.52) * mm});
            skLineSegment(sketch, "E26.4.3.1", {"start": v(-87.37, 28.52) * mm, "end": v(-85.33, 22.23) * mm});
            skLineSegment(sketch, "E26.4.3.2", {"start": v(-88.63, 32.4) * mm, "end": v(-82.02, 32.4) * mm});
            skLineSegment(sketch, "E26.4.3.3", {"start": v(-93.99, 28.52) * mm, "end": v(-99.34, 32.4) * mm});
            skLineSegment(sketch, "E26.4.3.4", {"start": v(-90.68, 26.11) * mm, "end": v(-96.03, 22.23) * mm});
            skLineSegment(sketch, "E26.4.3.5", {"start": v(-90.68, 38.7) * mm, "end": v(-88.63, 32.4) * mm});
            skLineSegment(sketch, "E26.4.3.6", {"start": v(-92.72, 32.4) * mm, "end": v(-90.68, 38.7) * mm});
            skLineSegment(sketch, "E26.4.3.7", {"start": v(-99.34, 32.4) * mm, "end": v(-92.72, 32.4) * mm});
            skLineSegment(sketch, "E26.4.3.8", {"start": v(-85.33, 22.23) * mm, "end": v(-90.68, 26.11) * mm});
            skLineSegment(sketch, "E26.4.3.9", {"start": v(-82.02, 32.4) * mm, "end": v(-87.37, 28.52) * mm});
            skLineSegment(sketch, "E26.4.4.0", {"start": v(-96.03, -3.68) * mm, "end": v(-93.99, 2.6) * mm});
            skLineSegment(sketch, "E26.4.4.1", {"start": v(-87.37, 2.6) * mm, "end": v(-85.33, -3.68) * mm});
            skLineSegment(sketch, "E26.4.4.2", {"start": v(-88.63, 6.5) * mm, "end": v(-82.02, 6.5) * mm});
            skLineSegment(sketch, "E26.4.4.3", {"start": v(-93.99, 2.6) * mm, "end": v(-99.34, 6.5) * mm});
            skLineSegment(sketch, "E26.4.4.4", {"start": v(-90.68, 0.2) * mm, "end": v(-96.03, -3.68) * mm});
            skLineSegment(sketch, "E26.4.4.5", {"start": v(-90.68, 12.79) * mm, "end": v(-88.63, 6.5) * mm});
            skLineSegment(sketch, "E26.4.4.6", {"start": v(-92.72, 6.5) * mm, "end": v(-90.68, 12.79) * mm});
            skLineSegment(sketch, "E26.4.4.7", {"start": v(-99.34, 6.5) * mm, "end": v(-92.72, 6.5) * mm});
            skLineSegment(sketch, "E26.4.4.8", {"start": v(-85.33, -3.68) * mm, "end": v(-90.68, 0.2) * mm});
            skLineSegment(sketch, "E26.4.4.9", {"start": v(-82.02, 6.5) * mm, "end": v(-87.37, 2.6) * mm});
            skLineSegment(sketch, "E26.5.0.0", {"start": v(-65.3, 99.95) * mm, "end": v(-63.25, 106.24) * mm});
            skLineSegment(sketch, "E26.5.0.1", {"start": v(-56.64, 106.24) * mm, "end": v(-54.6, 99.95) * mm});
            skLineSegment(sketch, "E26.5.0.2", {"start": v(-57.9, 110.13) * mm, "end": v(-51.28, 110.13) * mm});
            skLineSegment(sketch, "E26.5.0.3", {"start": v(-63.25, 106.24) * mm, "end": v(-68.6, 110.13) * mm});
            skLineSegment(sketch, "E26.5.0.4", {"start": v(-59.94, 103.84) * mm, "end": v(-65.3, 99.95) * mm});
            skLineSegment(sketch, "E26.5.0.5", {"start": v(-59.94, 116.42) * mm, "end": v(-57.9, 110.13) * mm});
            skLineSegment(sketch, "E26.5.0.6", {"start": v(-61.99, 110.13) * mm, "end": v(-59.94, 116.42) * mm});
            skLineSegment(sketch, "E26.5.0.7", {"start": v(-68.6, 110.13) * mm, "end": v(-61.99, 110.13) * mm});
            skLineSegment(sketch, "E26.5.0.8", {"start": v(-54.6, 99.95) * mm, "end": v(-59.94, 103.84) * mm});
            skLineSegment(sketch, "E26.5.0.9", {"start": v(-51.28, 110.13) * mm, "end": v(-56.64, 106.24) * mm});
            skLineSegment(sketch, "E26.5.1.0", {"start": v(-65.3, 74.04) * mm, "end": v(-63.25, 80.33) * mm});
            skLineSegment(sketch, "E26.5.1.1", {"start": v(-56.64, 80.33) * mm, "end": v(-54.6, 74.04) * mm});
            skLineSegment(sketch, "E26.5.1.2", {"start": v(-57.9, 84.22) * mm, "end": v(-51.28, 84.22) * mm});
            skLineSegment(sketch, "E26.5.1.3", {"start": v(-63.25, 80.33) * mm, "end": v(-68.6, 84.22) * mm});
            skLineSegment(sketch, "E26.5.1.4", {"start": v(-59.94, 77.93) * mm, "end": v(-65.3, 74.04) * mm});
            skLineSegment(sketch, "E26.5.1.5", {"start": v(-59.94, 90.51) * mm, "end": v(-57.9, 84.22) * mm});
            skLineSegment(sketch, "E26.5.1.6", {"start": v(-61.99, 84.22) * mm, "end": v(-59.94, 90.51) * mm});
            skLineSegment(sketch, "E26.5.1.7", {"start": v(-68.6, 84.22) * mm, "end": v(-61.99, 84.22) * mm});
            skLineSegment(sketch, "E26.5.1.8", {"start": v(-54.6, 74.04) * mm, "end": v(-59.94, 77.93) * mm});
            skLineSegment(sketch, "E26.5.1.9", {"start": v(-51.28, 84.22) * mm, "end": v(-56.64, 80.33) * mm});
            skLineSegment(sketch, "E26.5.2.0", {"start": v(-65.3, 48.13) * mm, "end": v(-63.25, 54.42) * mm});
            skLineSegment(sketch, "E26.5.2.1", {"start": v(-56.64, 54.42) * mm, "end": v(-54.6, 48.13) * mm});
            skLineSegment(sketch, "E26.5.2.2", {"start": v(-57.9, 58.31) * mm, "end": v(-51.28, 58.31) * mm});
            skLineSegment(sketch, "E26.5.2.3", {"start": v(-63.25, 54.42) * mm, "end": v(-68.6, 58.31) * mm});
            skLineSegment(sketch, "E26.5.2.4", {"start": v(-59.94, 52.02) * mm, "end": v(-65.3, 48.13) * mm});
            skLineSegment(sketch, "E26.5.2.5", {"start": v(-59.94, 64.6) * mm, "end": v(-57.9, 58.31) * mm});
            skLineSegment(sketch, "E26.5.2.6", {"start": v(-61.99, 58.31) * mm, "end": v(-59.94, 64.6) * mm});
            skLineSegment(sketch, "E26.5.2.7", {"start": v(-68.6, 58.31) * mm, "end": v(-61.99, 58.31) * mm});
            skLineSegment(sketch, "E26.5.2.8", {"start": v(-54.6, 48.13) * mm, "end": v(-59.94, 52.02) * mm});
            skLineSegment(sketch, "E26.5.2.9", {"start": v(-51.28, 58.31) * mm, "end": v(-56.64, 54.42) * mm});
            skLineSegment(sketch, "E26.5.3.0", {"start": v(-65.3, 22.23) * mm, "end": v(-63.25, 28.52) * mm});
            skLineSegment(sketch, "E26.5.3.1", {"start": v(-56.64, 28.52) * mm, "end": v(-54.6, 22.23) * mm});
            skLineSegment(sketch, "E26.5.3.2", {"start": v(-57.9, 32.4) * mm, "end": v(-51.28, 32.4) * mm});
            skLineSegment(sketch, "E26.5.3.3", {"start": v(-63.25, 28.52) * mm, "end": v(-68.6, 32.4) * mm});
            skLineSegment(sketch, "E26.5.3.4", {"start": v(-59.94, 26.11) * mm, "end": v(-65.3, 22.23) * mm});
            skLineSegment(sketch, "E26.5.3.5", {"start": v(-59.94, 38.7) * mm, "end": v(-57.9, 32.4) * mm});
            skLineSegment(sketch, "E26.5.3.6", {"start": v(-61.99, 32.4) * mm, "end": v(-59.94, 38.7) * mm});
            skLineSegment(sketch, "E26.5.3.7", {"start": v(-68.6, 32.4) * mm, "end": v(-61.99, 32.4) * mm});
            skLineSegment(sketch, "E26.5.3.8", {"start": v(-54.6, 22.23) * mm, "end": v(-59.94, 26.11) * mm});
            skLineSegment(sketch, "E26.5.3.9", {"start": v(-51.28, 32.4) * mm, "end": v(-56.64, 28.52) * mm});
            skLineSegment(sketch, "E26.5.4.0", {"start": v(-65.3, -3.68) * mm, "end": v(-63.25, 2.6) * mm});
            skLineSegment(sketch, "E26.5.4.1", {"start": v(-56.64, 2.6) * mm, "end": v(-54.6, -3.68) * mm});
            skLineSegment(sketch, "E26.5.4.2", {"start": v(-57.9, 6.5) * mm, "end": v(-51.28, 6.5) * mm});
            skLineSegment(sketch, "E26.5.4.3", {"start": v(-63.25, 2.6) * mm, "end": v(-68.6, 6.5) * mm});
            skLineSegment(sketch, "E26.5.4.4", {"start": v(-59.94, 0.2) * mm, "end": v(-65.3, -3.68) * mm});
            skLineSegment(sketch, "E26.5.4.5", {"start": v(-59.94, 12.79) * mm, "end": v(-57.9, 6.5) * mm});
            skLineSegment(sketch, "E26.5.4.6", {"start": v(-61.99, 6.5) * mm, "end": v(-59.94, 12.79) * mm});
            skLineSegment(sketch, "E26.5.4.7", {"start": v(-68.6, 6.5) * mm, "end": v(-61.99, 6.5) * mm});
            skLineSegment(sketch, "E26.5.4.8", {"start": v(-54.6, -3.68) * mm, "end": v(-59.94, 0.2) * mm});
            skLineSegment(sketch, "E26.5.4.9", {"start": v(-51.28, 6.5) * mm, "end": v(-56.64, 2.6) * mm});
            skLineSegment(sketch, "E26.direction1", {"start": v(-218.97, 99.95) * mm, "end": v(-188.23, 99.95) * mm, "construction": true});
            skLineSegment(sketch, "E26.direction2", {"start": v(-218.97, 99.95) * mm, "end": v(-218.97, 74.04) * mm, "construction": true});
            skLineSegment(sketch, "E27.bottom", {"start": v(-228.6, 120.27) * mm, "end": v(-198.37, 120.27) * mm});
            skLineSegment(sketch, "E27.left", {"start": v(-228.6, 120.27) * mm, "end": v(-228.6, 94.36) * mm});
            skLineSegment(sketch, "E28", {"start": v(-198.37, 103.47) * mm, "end": v(-200.42, 97.17) * mm});
            skLineSegment(sketch, "E29", {"start": v(-203.73, 87) * mm, "end": v(-198.37, 90.88) * mm});
            skLineSegment(sketch, "E30", {"start": v(-189.71, 97.17) * mm, "end": v(-196.33, 97.17) * mm});
            skLineSegment(sketch, "E31", {"start": v(-207.03, 97.17) * mm, "end": v(-201.68, 93.29) * mm});
            skLineSegment(sketch, "E32", {"start": v(-193.02, 87) * mm, "end": v(-195.07, 93.29) * mm});
            skLineSegment(sketch, "E33.trimOffspring", {"start": v(-196.33, 97.17) * mm, "end": v(-198.37, 103.47) * mm});
            skLineSegment(sketch, "E34.trimOffspring", {"start": v(-200.42, 97.17) * mm, "end": v(-207.03, 97.17) * mm});
            skLineSegment(sketch, "E35.trimOffspring", {"start": v(-201.68, 93.29) * mm, "end": v(-203.73, 87) * mm});
            skLineSegment(sketch, "E36.trimOffspring", {"start": v(-198.37, 90.88) * mm, "end": v(-193.02, 87) * mm});
            skLineSegment(sketch, "E37.trimOffspring", {"start": v(-195.07, 93.29) * mm, "end": v(-189.71, 97.17) * mm});
            skLineSegment(sketch, "E38.0.1.0", {"start": v(-198.37, 64.98) * mm, "end": v(-193.02, 61.09) * mm});
            skLineSegment(sketch, "E38.0.1.1", {"start": v(-195.07, 67.38) * mm, "end": v(-189.71, 71.27) * mm});
            skLineSegment(sketch, "E38.0.1.2", {"start": v(-193.02, 61.09) * mm, "end": v(-195.07, 67.38) * mm});
            skLineSegment(sketch, "E38.0.1.3", {"start": v(-201.68, 67.38) * mm, "end": v(-203.73, 61.09) * mm});
            skLineSegment(sketch, "E38.0.1.4", {"start": v(-189.71, 71.27) * mm, "end": v(-196.33, 71.27) * mm});
            skLineSegment(sketch, "E38.0.1.5", {"start": v(-203.73, 61.09) * mm, "end": v(-198.37, 64.98) * mm});
            skLineSegment(sketch, "E38.0.1.6", {"start": v(-200.42, 71.27) * mm, "end": v(-207.03, 71.27) * mm});
            skLineSegment(sketch, "E38.0.1.7", {"start": v(-207.03, 71.27) * mm, "end": v(-201.68, 67.38) * mm});
            skLineSegment(sketch, "E38.0.1.8", {"start": v(-198.37, 77.56) * mm, "end": v(-200.42, 71.27) * mm});
            skLineSegment(sketch, "E38.0.1.9", {"start": v(-196.33, 71.27) * mm, "end": v(-198.37, 77.56) * mm});
            skLineSegment(sketch, "E38.0.2.0", {"start": v(-198.37, 39.07) * mm, "end": v(-193.02, 35.18) * mm});
            skLineSegment(sketch, "E38.0.2.1", {"start": v(-195.07, 41.47) * mm, "end": v(-189.71, 45.36) * mm});
            skLineSegment(sketch, "E38.0.2.2", {"start": v(-193.02, 35.18) * mm, "end": v(-195.07, 41.47) * mm});
            skLineSegment(sketch, "E38.0.2.3", {"start": v(-201.68, 41.47) * mm, "end": v(-203.73, 35.18) * mm});
            skLineSegment(sketch, "E38.0.2.4", {"start": v(-189.71, 45.36) * mm, "end": v(-196.33, 45.36) * mm});
            skLineSegment(sketch, "E38.0.2.5", {"start": v(-203.73, 35.18) * mm, "end": v(-198.37, 39.07) * mm});
            skLineSegment(sketch, "E38.0.2.6", {"start": v(-200.42, 45.36) * mm, "end": v(-207.03, 45.36) * mm});
            skLineSegment(sketch, "E38.0.2.7", {"start": v(-207.03, 45.36) * mm, "end": v(-201.68, 41.47) * mm});
            skLineSegment(sketch, "E38.0.2.8", {"start": v(-198.37, 51.65) * mm, "end": v(-200.42, 45.36) * mm});
            skLineSegment(sketch, "E38.0.2.9", {"start": v(-196.33, 45.36) * mm, "end": v(-198.37, 51.65) * mm});
            skLineSegment(sketch, "E38.0.3.0", {"start": v(-198.37, 13.16) * mm, "end": v(-193.02, 9.27) * mm});
            skLineSegment(sketch, "E38.0.3.1", {"start": v(-195.07, 15.56) * mm, "end": v(-189.71, 19.45) * mm});
            skLineSegment(sketch, "E38.0.3.2", {"start": v(-193.02, 9.27) * mm, "end": v(-195.07, 15.56) * mm});
            skLineSegment(sketch, "E38.0.3.3", {"start": v(-201.68, 15.56) * mm, "end": v(-203.73, 9.27) * mm});
            skLineSegment(sketch, "E38.0.3.4", {"start": v(-189.71, 19.45) * mm, "end": v(-196.33, 19.45) * mm});
            skLineSegment(sketch, "E38.0.3.5", {"start": v(-203.73, 9.27) * mm, "end": v(-198.37, 13.16) * mm});
            skLineSegment(sketch, "E38.0.3.6", {"start": v(-200.42, 19.45) * mm, "end": v(-207.03, 19.45) * mm});
            skLineSegment(sketch, "E38.0.3.7", {"start": v(-207.03, 19.45) * mm, "end": v(-201.68, 15.56) * mm});
            skLineSegment(sketch, "E38.0.3.8", {"start": v(-198.37, 25.74) * mm, "end": v(-200.42, 19.45) * mm});
            skLineSegment(sketch, "E38.0.3.9", {"start": v(-196.33, 19.45) * mm, "end": v(-198.37, 25.74) * mm});
            skLineSegment(sketch, "E38.1.0.0", {"start": v(-167.64, 90.88) * mm, "end": v(-162.29, 87) * mm});
            skLineSegment(sketch, "E38.1.0.1", {"start": v(-164.33, 93.29) * mm, "end": v(-158.98, 97.17) * mm});
            skLineSegment(sketch, "E38.1.0.2", {"start": v(-162.29, 87) * mm, "end": v(-164.33, 93.29) * mm});
            skLineSegment(sketch, "E38.1.0.3", {"start": v(-170.95, 93.29) * mm, "end": v(-173, 87) * mm});
            skLineSegment(sketch, "E38.1.0.4", {"start": v(-158.98, 97.17) * mm, "end": v(-165.6, 97.17) * mm});
            skLineSegment(sketch, "E38.1.0.5", {"start": v(-173, 87) * mm, "end": v(-167.64, 90.88) * mm});
            skLineSegment(sketch, "E38.1.0.6", {"start": v(-169.68, 97.17) * mm, "end": v(-176.3, 97.17) * mm});
            skLineSegment(sketch, "E38.1.0.7", {"start": v(-176.3, 97.17) * mm, "end": v(-170.95, 93.29) * mm});
            skLineSegment(sketch, "E38.1.0.8", {"start": v(-167.64, 103.47) * mm, "end": v(-169.68, 97.17) * mm});
            skLineSegment(sketch, "E38.1.0.9", {"start": v(-165.6, 97.17) * mm, "end": v(-167.64, 103.47) * mm});
            skLineSegment(sketch, "E38.1.1.0", {"start": v(-167.64, 64.98) * mm, "end": v(-162.29, 61.09) * mm});
            skLineSegment(sketch, "E38.1.1.1", {"start": v(-164.33, 67.38) * mm, "end": v(-158.98, 71.27) * mm});
            skLineSegment(sketch, "E38.1.1.2", {"start": v(-162.29, 61.09) * mm, "end": v(-164.33, 67.38) * mm});
            skLineSegment(sketch, "E38.1.1.3", {"start": v(-170.95, 67.38) * mm, "end": v(-173, 61.09) * mm});
            skLineSegment(sketch, "E38.1.1.4", {"start": v(-158.98, 71.27) * mm, "end": v(-165.6, 71.27) * mm});
            skLineSegment(sketch, "E38.1.1.5", {"start": v(-173, 61.09) * mm, "end": v(-167.64, 64.98) * mm});
            skLineSegment(sketch, "E38.1.1.6", {"start": v(-169.68, 71.27) * mm, "end": v(-176.3, 71.27) * mm});
            skLineSegment(sketch, "E38.1.1.7", {"start": v(-176.3, 71.27) * mm, "end": v(-170.95, 67.38) * mm});
            skLineSegment(sketch, "E38.1.1.8", {"start": v(-167.64, 77.56) * mm, "end": v(-169.68, 71.27) * mm});
            skLineSegment(sketch, "E38.1.1.9", {"start": v(-165.6, 71.27) * mm, "end": v(-167.64, 77.56) * mm});
            skLineSegment(sketch, "E38.1.2.0", {"start": v(-167.64, 39.07) * mm, "end": v(-162.29, 35.18) * mm});
            skLineSegment(sketch, "E38.1.2.1", {"start": v(-164.33, 41.47) * mm, "end": v(-158.98, 45.36) * mm});
            skLineSegment(sketch, "E38.1.2.2", {"start": v(-162.29, 35.18) * mm, "end": v(-164.33, 41.47) * mm});
            skLineSegment(sketch, "E38.1.2.3", {"start": v(-170.95, 41.47) * mm, "end": v(-173, 35.18) * mm});
            skLineSegment(sketch, "E38.1.2.4", {"start": v(-158.98, 45.36) * mm, "end": v(-165.6, 45.36) * mm});
            skLineSegment(sketch, "E38.1.2.5", {"start": v(-173, 35.18) * mm, "end": v(-167.64, 39.07) * mm});
            skLineSegment(sketch, "E38.1.2.6", {"start": v(-169.68, 45.36) * mm, "end": v(-176.3, 45.36) * mm});
            skLineSegment(sketch, "E38.1.2.7", {"start": v(-176.3, 45.36) * mm, "end": v(-170.95, 41.47) * mm});
            skLineSegment(sketch, "E38.1.2.8", {"start": v(-167.64, 51.65) * mm, "end": v(-169.68, 45.36) * mm});
            skLineSegment(sketch, "E38.1.2.9", {"start": v(-165.6, 45.36) * mm, "end": v(-167.64, 51.65) * mm});
            skLineSegment(sketch, "E38.1.3.0", {"start": v(-167.64, 13.16) * mm, "end": v(-162.29, 9.27) * mm});
            skLineSegment(sketch, "E38.1.3.1", {"start": v(-164.33, 15.56) * mm, "end": v(-158.98, 19.45) * mm});
            skLineSegment(sketch, "E38.1.3.2", {"start": v(-162.29, 9.27) * mm, "end": v(-164.33, 15.56) * mm});
            skLineSegment(sketch, "E38.1.3.3", {"start": v(-170.95, 15.56) * mm, "end": v(-173, 9.27) * mm});
            skLineSegment(sketch, "E38.1.3.4", {"start": v(-158.98, 19.45) * mm, "end": v(-165.6, 19.45) * mm});
            skLineSegment(sketch, "E38.1.3.5", {"start": v(-173, 9.27) * mm, "end": v(-167.64, 13.16) * mm});
            skLineSegment(sketch, "E38.1.3.6", {"start": v(-169.68, 19.45) * mm, "end": v(-176.3, 19.45) * mm});
            skLineSegment(sketch, "E38.1.3.7", {"start": v(-176.3, 19.45) * mm, "end": v(-170.95, 15.56) * mm});
            skLineSegment(sketch, "E38.1.3.8", {"start": v(-167.64, 25.74) * mm, "end": v(-169.68, 19.45) * mm});
            skLineSegment(sketch, "E38.1.3.9", {"start": v(-165.6, 19.45) * mm, "end": v(-167.64, 25.74) * mm});
            skLineSegment(sketch, "E38.2.0.0", {"start": v(-136.9, 90.88) * mm, "end": v(-131.55, 87) * mm});
            skLineSegment(sketch, "E38.2.0.1", {"start": v(-133.6, 93.29) * mm, "end": v(-128.25, 97.17) * mm});
            skLineSegment(sketch, "E38.2.0.2", {"start": v(-131.55, 87) * mm, "end": v(-133.6, 93.29) * mm});
            skLineSegment(sketch, "E38.2.0.3", {"start": v(-140.21, 93.29) * mm, "end": v(-142.26, 87) * mm});
            skLineSegment(sketch, "E38.2.0.4", {"start": v(-128.25, 97.17) * mm, "end": v(-134.86, 97.17) * mm});
            skLineSegment(sketch, "E38.2.0.5", {"start": v(-142.26, 87) * mm, "end": v(-136.9, 90.88) * mm});
            skLineSegment(sketch, "E38.2.0.6", {"start": v(-138.95, 97.17) * mm, "end": v(-145.57, 97.17) * mm});
            skLineSegment(sketch, "E38.2.0.7", {"start": v(-145.57, 97.17) * mm, "end": v(-140.21, 93.29) * mm});
            skLineSegment(sketch, "E38.2.0.8", {"start": v(-136.9, 103.47) * mm, "end": v(-138.95, 97.17) * mm});
            skLineSegment(sketch, "E38.2.0.9", {"start": v(-134.86, 97.17) * mm, "end": v(-136.9, 103.47) * mm});
            skLineSegment(sketch, "E38.2.1.0", {"start": v(-136.9, 64.98) * mm, "end": v(-131.55, 61.09) * mm});
            skLineSegment(sketch, "E38.2.1.1", {"start": v(-133.6, 67.38) * mm, "end": v(-128.25, 71.27) * mm});
            skLineSegment(sketch, "E38.2.1.2", {"start": v(-131.55, 61.09) * mm, "end": v(-133.6, 67.38) * mm});
            skLineSegment(sketch, "E38.2.1.3", {"start": v(-140.21, 67.38) * mm, "end": v(-142.26, 61.09) * mm});
            skLineSegment(sketch, "E38.2.1.4", {"start": v(-128.25, 71.27) * mm, "end": v(-134.86, 71.27) * mm});
            skLineSegment(sketch, "E38.2.1.5", {"start": v(-142.26, 61.09) * mm, "end": v(-136.9, 64.98) * mm});
            skLineSegment(sketch, "E38.2.1.6", {"start": v(-138.95, 71.27) * mm, "end": v(-145.57, 71.27) * mm});
            skLineSegment(sketch, "E38.2.1.7", {"start": v(-145.57, 71.27) * mm, "end": v(-140.21, 67.38) * mm});
            skLineSegment(sketch, "E38.2.1.8", {"start": v(-136.9, 77.56) * mm, "end": v(-138.95, 71.27) * mm});
            skLineSegment(sketch, "E38.2.1.9", {"start": v(-134.86, 71.27) * mm, "end": v(-136.9, 77.56) * mm});
            skLineSegment(sketch, "E38.2.2.0", {"start": v(-136.9, 39.07) * mm, "end": v(-131.55, 35.18) * mm});
            skLineSegment(sketch, "E38.2.2.1", {"start": v(-133.6, 41.47) * mm, "end": v(-128.25, 45.36) * mm});
            skLineSegment(sketch, "E38.2.2.2", {"start": v(-131.55, 35.18) * mm, "end": v(-133.6, 41.47) * mm});
            skLineSegment(sketch, "E38.2.2.3", {"start": v(-140.21, 41.47) * mm, "end": v(-142.26, 35.18) * mm});
            skLineSegment(sketch, "E38.2.2.4", {"start": v(-128.25, 45.36) * mm, "end": v(-134.86, 45.36) * mm});
            skLineSegment(sketch, "E38.2.2.5", {"start": v(-142.26, 35.18) * mm, "end": v(-136.9, 39.07) * mm});
            skLineSegment(sketch, "E38.2.2.6", {"start": v(-138.95, 45.36) * mm, "end": v(-145.57, 45.36) * mm});
            skLineSegment(sketch, "E38.2.2.7", {"start": v(-145.57, 45.36) * mm, "end": v(-140.21, 41.47) * mm});
            skLineSegment(sketch, "E38.2.2.8", {"start": v(-136.9, 51.65) * mm, "end": v(-138.95, 45.36) * mm});
            skLineSegment(sketch, "E38.2.2.9", {"start": v(-134.86, 45.36) * mm, "end": v(-136.9, 51.65) * mm});
            skLineSegment(sketch, "E38.2.3.0", {"start": v(-136.9, 13.16) * mm, "end": v(-131.55, 9.27) * mm});
            skLineSegment(sketch, "E38.2.3.1", {"start": v(-133.6, 15.56) * mm, "end": v(-128.25, 19.45) * mm});
            skLineSegment(sketch, "E38.2.3.2", {"start": v(-131.55, 9.27) * mm, "end": v(-133.6, 15.56) * mm});
            skLineSegment(sketch, "E38.2.3.3", {"start": v(-140.21, 15.56) * mm, "end": v(-142.26, 9.27) * mm});
            skLineSegment(sketch, "E38.2.3.4", {"start": v(-128.25, 19.45) * mm, "end": v(-134.86, 19.45) * mm});
            skLineSegment(sketch, "E38.2.3.5", {"start": v(-142.26, 9.27) * mm, "end": v(-136.9, 13.16) * mm});
            skLineSegment(sketch, "E38.2.3.6", {"start": v(-138.95, 19.45) * mm, "end": v(-145.57, 19.45) * mm});
            skLineSegment(sketch, "E38.2.3.7", {"start": v(-145.57, 19.45) * mm, "end": v(-140.21, 15.56) * mm});
            skLineSegment(sketch, "E38.2.3.8", {"start": v(-136.9, 25.74) * mm, "end": v(-138.95, 19.45) * mm});
            skLineSegment(sketch, "E38.2.3.9", {"start": v(-134.86, 19.45) * mm, "end": v(-136.9, 25.74) * mm});
            skLineSegment(sketch, "E38.3.0.0", {"start": v(-106.17, 90.88) * mm, "end": v(-100.82, 87) * mm});
            skLineSegment(sketch, "E38.3.0.1", {"start": v(-102.86, 93.29) * mm, "end": v(-97.51, 97.17) * mm});
            skLineSegment(sketch, "E38.3.0.2", {"start": v(-100.82, 87) * mm, "end": v(-102.86, 93.29) * mm});
            skLineSegment(sketch, "E38.3.0.3", {"start": v(-109.48, 93.29) * mm, "end": v(-111.52, 87) * mm});
            skLineSegment(sketch, "E38.3.0.4", {"start": v(-97.51, 97.17) * mm, "end": v(-104.13, 97.17) * mm});
            skLineSegment(sketch, "E38.3.0.5", {"start": v(-111.52, 87) * mm, "end": v(-106.17, 90.88) * mm});
            skLineSegment(sketch, "E38.3.0.6", {"start": v(-108.22, 97.17) * mm, "end": v(-114.83, 97.17) * mm});
            skLineSegment(sketch, "E38.3.0.7", {"start": v(-114.83, 97.17) * mm, "end": v(-109.48, 93.29) * mm});
            skLineSegment(sketch, "E38.3.0.8", {"start": v(-106.17, 103.47) * mm, "end": v(-108.22, 97.17) * mm});
            skLineSegment(sketch, "E38.3.0.9", {"start": v(-104.13, 97.17) * mm, "end": v(-106.17, 103.47) * mm});
            skLineSegment(sketch, "E38.3.1.0", {"start": v(-106.17, 64.98) * mm, "end": v(-100.82, 61.09) * mm});
            skLineSegment(sketch, "E38.3.1.1", {"start": v(-102.86, 67.38) * mm, "end": v(-97.51, 71.27) * mm});
            skLineSegment(sketch, "E38.3.1.2", {"start": v(-100.82, 61.09) * mm, "end": v(-102.86, 67.38) * mm});
            skLineSegment(sketch, "E38.3.1.3", {"start": v(-109.48, 67.38) * mm, "end": v(-111.52, 61.09) * mm});
            skLineSegment(sketch, "E38.3.1.4", {"start": v(-97.51, 71.27) * mm, "end": v(-104.13, 71.27) * mm});
            skLineSegment(sketch, "E38.3.1.5", {"start": v(-111.52, 61.09) * mm, "end": v(-106.17, 64.98) * mm});
            skLineSegment(sketch, "E38.3.1.6", {"start": v(-108.22, 71.27) * mm, "end": v(-114.83, 71.27) * mm});
            skLineSegment(sketch, "E38.3.1.7", {"start": v(-114.83, 71.27) * mm, "end": v(-109.48, 67.38) * mm});
            skLineSegment(sketch, "E38.3.1.8", {"start": v(-106.17, 77.56) * mm, "end": v(-108.22, 71.27) * mm});
            skLineSegment(sketch, "E38.3.1.9", {"start": v(-104.13, 71.27) * mm, "end": v(-106.17, 77.56) * mm});
            skLineSegment(sketch, "E38.3.2.0", {"start": v(-106.17, 39.07) * mm, "end": v(-100.82, 35.18) * mm});
            skLineSegment(sketch, "E38.3.2.1", {"start": v(-102.86, 41.47) * mm, "end": v(-97.51, 45.36) * mm});
            skLineSegment(sketch, "E38.3.2.2", {"start": v(-100.82, 35.18) * mm, "end": v(-102.86, 41.47) * mm});
            skLineSegment(sketch, "E38.3.2.3", {"start": v(-109.48, 41.47) * mm, "end": v(-111.52, 35.18) * mm});
            skLineSegment(sketch, "E38.3.2.4", {"start": v(-97.51, 45.36) * mm, "end": v(-104.13, 45.36) * mm});
            skLineSegment(sketch, "E38.3.2.5", {"start": v(-111.52, 35.18) * mm, "end": v(-106.17, 39.07) * mm});
            skLineSegment(sketch, "E38.3.2.6", {"start": v(-108.22, 45.36) * mm, "end": v(-114.83, 45.36) * mm});
            skLineSegment(sketch, "E38.3.2.7", {"start": v(-114.83, 45.36) * mm, "end": v(-109.48, 41.47) * mm});
            skLineSegment(sketch, "E38.3.2.8", {"start": v(-106.17, 51.65) * mm, "end": v(-108.22, 45.36) * mm});
            skLineSegment(sketch, "E38.3.2.9", {"start": v(-104.13, 45.36) * mm, "end": v(-106.17, 51.65) * mm});
            skLineSegment(sketch, "E38.3.3.0", {"start": v(-106.17, 13.16) * mm, "end": v(-100.82, 9.27) * mm});
            skLineSegment(sketch, "E38.3.3.1", {"start": v(-102.86, 15.56) * mm, "end": v(-97.51, 19.45) * mm});
            skLineSegment(sketch, "E38.3.3.2", {"start": v(-100.82, 9.27) * mm, "end": v(-102.86, 15.56) * mm});
            skLineSegment(sketch, "E38.3.3.3", {"start": v(-109.48, 15.56) * mm, "end": v(-111.52, 9.27) * mm});
            skLineSegment(sketch, "E38.3.3.4", {"start": v(-97.51, 19.45) * mm, "end": v(-104.13, 19.45) * mm});
            skLineSegment(sketch, "E38.3.3.5", {"start": v(-111.52, 9.27) * mm, "end": v(-106.17, 13.16) * mm});
            skLineSegment(sketch, "E38.3.3.6", {"start": v(-108.22, 19.45) * mm, "end": v(-114.83, 19.45) * mm});
            skLineSegment(sketch, "E38.3.3.7", {"start": v(-114.83, 19.45) * mm, "end": v(-109.48, 15.56) * mm});
            skLineSegment(sketch, "E38.3.3.8", {"start": v(-106.17, 25.74) * mm, "end": v(-108.22, 19.45) * mm});
            skLineSegment(sketch, "E38.3.3.9", {"start": v(-104.13, 19.45) * mm, "end": v(-106.17, 25.74) * mm});
            skLineSegment(sketch, "E38.4.0.0", {"start": v(-75.44, 90.88) * mm, "end": v(-70.09, 87) * mm});
            skLineSegment(sketch, "E38.4.0.1", {"start": v(-72.13, 93.29) * mm, "end": v(-66.78, 97.17) * mm});
            skLineSegment(sketch, "E38.4.0.2", {"start": v(-70.09, 87) * mm, "end": v(-72.13, 93.29) * mm});
            skLineSegment(sketch, "E38.4.0.3", {"start": v(-78.75, 93.29) * mm, "end": v(-80.79, 87) * mm});
            skLineSegment(sketch, "E38.4.0.4", {"start": v(-66.78, 97.17) * mm, "end": v(-73.4, 97.17) * mm});
            skLineSegment(sketch, "E38.4.0.5", {"start": v(-80.79, 87) * mm, "end": v(-75.44, 90.88) * mm});
            skLineSegment(sketch, "E38.4.0.6", {"start": v(-77.48, 97.17) * mm, "end": v(-84.1, 97.17) * mm});
            skLineSegment(sketch, "E38.4.0.7", {"start": v(-84.1, 97.17) * mm, "end": v(-78.75, 93.29) * mm});
            skLineSegment(sketch, "E38.4.0.8", {"start": v(-75.44, 103.47) * mm, "end": v(-77.48, 97.17) * mm});
            skLineSegment(sketch, "E38.4.0.9", {"start": v(-73.4, 97.17) * mm, "end": v(-75.44, 103.47) * mm});
            skLineSegment(sketch, "E38.4.1.0", {"start": v(-75.44, 64.98) * mm, "end": v(-70.09, 61.09) * mm});
            skLineSegment(sketch, "E38.4.1.1", {"start": v(-72.13, 67.38) * mm, "end": v(-66.78, 71.27) * mm});
            skLineSegment(sketch, "E38.4.1.2", {"start": v(-70.09, 61.09) * mm, "end": v(-72.13, 67.38) * mm});
            skLineSegment(sketch, "E38.4.1.3", {"start": v(-78.75, 67.38) * mm, "end": v(-80.79, 61.09) * mm});
            skLineSegment(sketch, "E38.4.1.4", {"start": v(-66.78, 71.27) * mm, "end": v(-73.4, 71.27) * mm});
            skLineSegment(sketch, "E38.4.1.5", {"start": v(-80.79, 61.09) * mm, "end": v(-75.44, 64.98) * mm});
            skLineSegment(sketch, "E38.4.1.6", {"start": v(-77.48, 71.27) * mm, "end": v(-84.1, 71.27) * mm});
            skLineSegment(sketch, "E38.4.1.7", {"start": v(-84.1, 71.27) * mm, "end": v(-78.75, 67.38) * mm});
            skLineSegment(sketch, "E38.4.1.8", {"start": v(-75.44, 77.56) * mm, "end": v(-77.48, 71.27) * mm});
            skLineSegment(sketch, "E38.4.1.9", {"start": v(-73.4, 71.27) * mm, "end": v(-75.44, 77.56) * mm});
            skLineSegment(sketch, "E38.4.2.0", {"start": v(-75.44, 39.07) * mm, "end": v(-70.09, 35.18) * mm});
            skLineSegment(sketch, "E38.4.2.1", {"start": v(-72.13, 41.47) * mm, "end": v(-66.78, 45.36) * mm});
            skLineSegment(sketch, "E38.4.2.2", {"start": v(-70.09, 35.18) * mm, "end": v(-72.13, 41.47) * mm});
            skLineSegment(sketch, "E38.4.2.3", {"start": v(-78.75, 41.47) * mm, "end": v(-80.79, 35.18) * mm});
            skLineSegment(sketch, "E38.4.2.4", {"start": v(-66.78, 45.36) * mm, "end": v(-73.4, 45.36) * mm});
            skLineSegment(sketch, "E38.4.2.5", {"start": v(-80.79, 35.18) * mm, "end": v(-75.44, 39.07) * mm});
            skLineSegment(sketch, "E38.4.2.6", {"start": v(-77.48, 45.36) * mm, "end": v(-84.1, 45.36) * mm});
            skLineSegment(sketch, "E38.4.2.7", {"start": v(-84.1, 45.36) * mm, "end": v(-78.75, 41.47) * mm});
            skLineSegment(sketch, "E38.4.2.8", {"start": v(-75.44, 51.65) * mm, "end": v(-77.48, 45.36) * mm});
            skLineSegment(sketch, "E38.4.2.9", {"start": v(-73.4, 45.36) * mm, "end": v(-75.44, 51.65) * mm});
            skLineSegment(sketch, "E38.4.3.0", {"start": v(-75.44, 13.16) * mm, "end": v(-70.09, 9.27) * mm});
            skLineSegment(sketch, "E38.4.3.1", {"start": v(-72.13, 15.56) * mm, "end": v(-66.78, 19.45) * mm});
            skLineSegment(sketch, "E38.4.3.2", {"start": v(-70.09, 9.27) * mm, "end": v(-72.13, 15.56) * mm});
            skLineSegment(sketch, "E38.4.3.3", {"start": v(-78.75, 15.56) * mm, "end": v(-80.79, 9.27) * mm});
            skLineSegment(sketch, "E38.4.3.4", {"start": v(-66.78, 19.45) * mm, "end": v(-73.4, 19.45) * mm});
            skLineSegment(sketch, "E38.4.3.5", {"start": v(-80.79, 9.27) * mm, "end": v(-75.44, 13.16) * mm});
            skLineSegment(sketch, "E38.4.3.6", {"start": v(-77.48, 19.45) * mm, "end": v(-84.1, 19.45) * mm});
            skLineSegment(sketch, "E38.4.3.7", {"start": v(-84.1, 19.45) * mm, "end": v(-78.75, 15.56) * mm});
            skLineSegment(sketch, "E38.4.3.8", {"start": v(-75.44, 25.74) * mm, "end": v(-77.48, 19.45) * mm});
            skLineSegment(sketch, "E38.4.3.9", {"start": v(-73.4, 19.45) * mm, "end": v(-75.44, 25.74) * mm});
            skLineSegment(sketch, "E38.direction1", {"start": v(-198.37, 90.88) * mm, "end": v(-167.64, 90.88) * mm, "construction": true});
            skLineSegment(sketch, "E38.direction2", {"start": v(-198.37, 90.88) * mm, "end": v(-198.37, 64.98) * mm, "construction": true});
            skSolve(sketch);
        }
        {
            var Q0;
            {var subQ7=sQuery(id+"F2.wireOp",EDGE,"E1.bottom");Q0=makeQuery(id+"F2.imprint","IMPRINT",FACE,{"disambiguationData":[TD([[makeQuery(id+"F2.imprint","IMPRINT",EDGE,{"derivedFrom":subQ7}),1.0]])]});}
            var Q1;
            Q1=makeQuery(id+"F2.imprint","IMPRINT",FACE,{"disambiguationData":[TD([[makeQuery(id+"F2.imprint","IMPRINT",EDGE,{"derivedFrom":sQuery(id+"F2.wireOp",EDGE,"E2.bottom")}),1.0]])]});
            var Q2;
            {var subQ0=sQuery(id+"F2.wireOp",EDGE,"E3.MirrorCS");Q2=makeQuery(id+"F2.imprint","IMPRINT",FACE,{"disambiguationData":[TD([[makeQuery(id+"F2.imprint","IMPRINT",EDGE,{"derivedFrom":subQ0}),-1.0]])]});}
            var Q3;
            {var subQ0=sQuery(id+"F2.wireOp",EDGE,"E5.MirrorCS");Q3=makeQuery(id+"F2.imprint","IMPRINT",FACE,{"disambiguationData":[TD([[makeQuery(id+"F2.imprint","IMPRINT",EDGE,{"derivedFrom":subQ0}),-1.0]])]});}
            var Q4;
            {var subQ2=sQuery(id+"F2.wireOp",EDGE,"E7.MirrorCS");Q4=makeQuery(id+"F2.imprint","IMPRINT",FACE,{"disambiguationData":[TD([[makeQuery(id+"F2.imprint","IMPRINT",EDGE,{"derivedFrom":subQ2}),-1.0]])]});}
            var Q5;
            {var subQ0=sQuery(id+"F2.wireOp",EDGE,"E12.MirrorCS");Q5=makeQuery(id+"F2.imprint","IMPRINT",FACE,{"disambiguationData":[TD([[makeQuery(id+"F2.imprint","IMPRINT",EDGE,{"derivedFrom":subQ0}),1.0]])]});}
            var Q6;
            {var subQ0=sQuery(id+"F2.wireOp",EDGE,"E10.MirrorCS");Q6=makeQuery(id+"F2.imprint","IMPRINT",FACE,{"disambiguationData":[TD([[makeQuery(id+"F2.imprint","IMPRINT",EDGE,{"derivedFrom":subQ0}),1.0]])]});}
            var Q7;
            Q7=makeQuery(id+"F2.imprint","IMPRINT",FACE,{"disambiguationData":[TD([[makeQuery(id+"F2.imprint","IMPRINT",EDGE,{"derivedFrom":sQuery(id+"F2.wireOp",EDGE,"E9.bottom")}),-1.0]])]});
            extrude(context, id + "F3", {"entities" : qUnion([Q0, Q1, Q2, Q3, Q4, Q5, Q6, Q7]), "operationType" : NewBodyOperationType.ADD, "depth" : 9.52 * mm});
        }
    });
